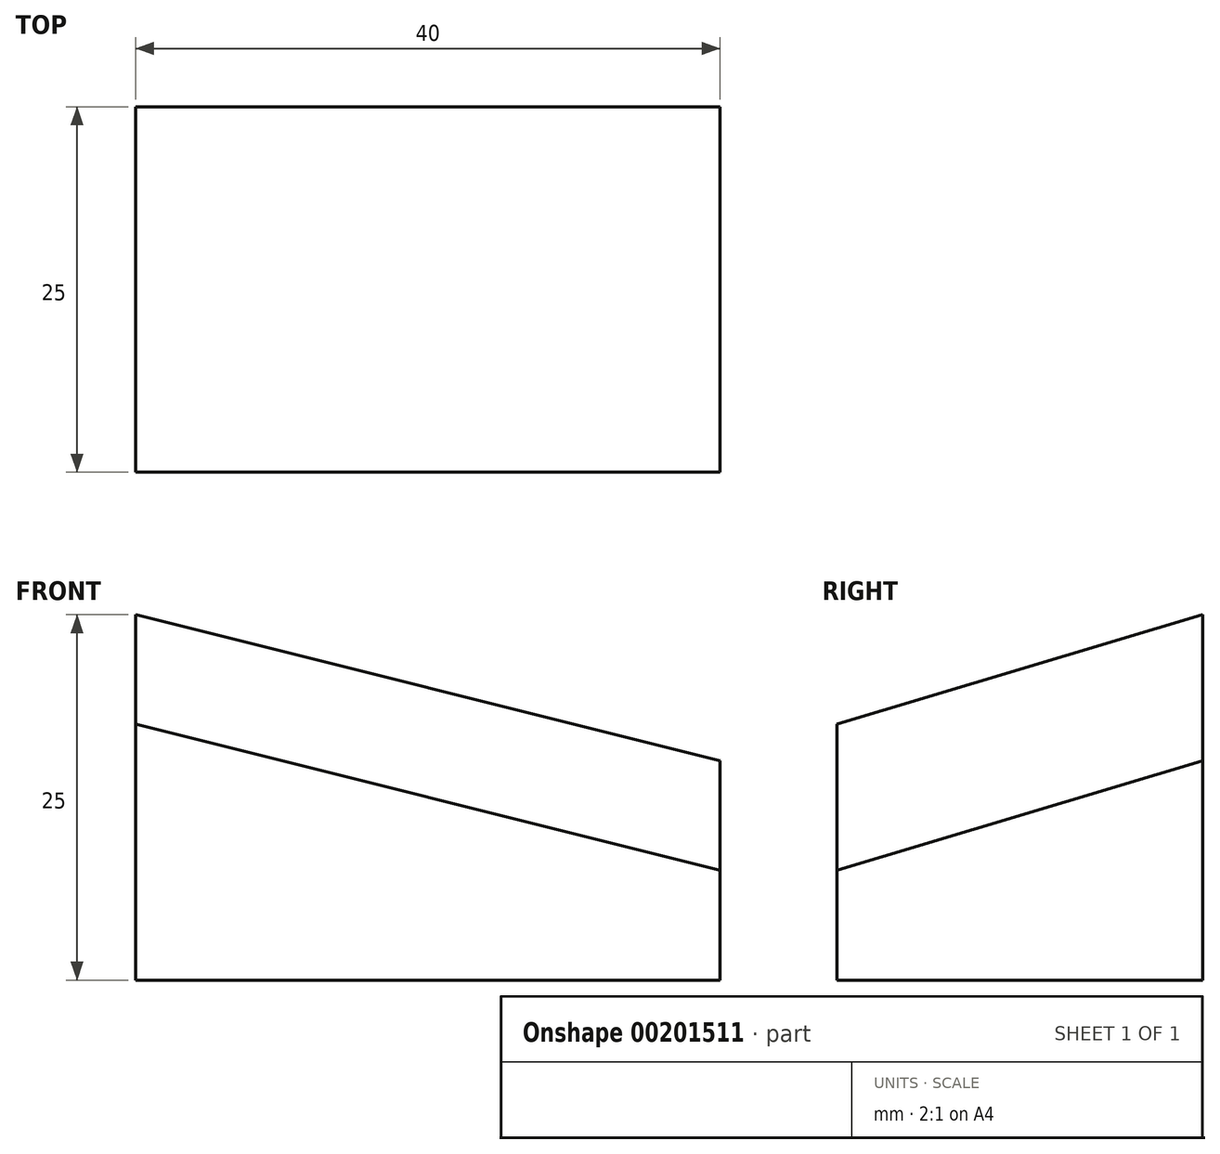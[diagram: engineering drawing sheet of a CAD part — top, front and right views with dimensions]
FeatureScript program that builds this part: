
annotation { "Feature Type Name" : "Feature", "Feature Type Description" : "" }
export const myFeature = defineFeature(function(context is Context, id is Id, definition is map)
    precondition{}
    {
        {
            var Q0;
            Q0=qCreatedBy(makeId("Front.planeOp"),FACE);
            var sketch = newSketch(context, id + "F0", { "sketchPlane" : qUnion([Q0])});
            skLineSegment(sketch, "E0", {"start": v(0, 0) * mm, "end": v(-40, 0) * mm});
            skLineSegment(sketch, "E1", {"start": v(-40, 0) * mm, "end": v(-40, 17.5) * mm});
            skLineSegment(sketch, "E2", {"start": v(-40, 17.5) * mm, "end": v(0, 7.5) * mm});
            skLineSegment(sketch, "E3", {"start": v(0, 7.5) * mm, "end": v(0, 0) * mm});
            skSolve(sketch);
        }
        {
            var Q0;
            Q0=qCreatedBy(makeId("Front.planeOp"),FACE);
            cPlane(context, id + "F1", {"entities" : qUnion([Q0]), "cplaneType" : CPlaneType.OFFSET, "offset" : 25 * mm, "oppositeDirection" : true, "width" : 150 * mm, "height" : 150 * mm});
        }
        {
            var Q0;
            Q0=qCreatedBy(id+"F1.planeOp",FACE);
            var sketch = newSketch(context, id + "F2", { "sketchPlane" : qUnion([Q0])});
            skLineSegment(sketch, "E4", {"start": v(0, 0) * mm, "end": v(-40, 0) * mm});
            skLineSegment(sketch, "E5", {"start": v(-40, 0) * mm, "end": v(-40, 25) * mm});
            skLineSegment(sketch, "E6", {"start": v(-40, 25) * mm, "end": v(0, 15) * mm});
            skLineSegment(sketch, "E7", {"start": v(0, 15) * mm, "end": v(0, 0) * mm});
            skSolve(sketch);
        }
        {
            var Q0;
            Q0=makeQuery(id+"F0.imprint","IMPRINT",FACE,{"disambiguationData":[TD([[makeQuery(id+"F0.imprint","IMPRINT",EDGE,{"derivedFrom":sQuery(id+"F0.wireOp",EDGE,"E0")}),-1.0]])]});
            var Q1;
            Q1=makeQuery(id+"F2.imprint","IMPRINT",FACE,{"disambiguationData":[TD([[makeQuery(id+"F2.imprint","IMPRINT",EDGE,{"derivedFrom":sQuery(id+"F2.wireOp",EDGE,"E4")}),-1.0]])]});
            loft(context, id + "F3", {"sheetProfilesArray" : [{ "sheetProfileEntities" : qUnion([Q0]) }, { "sheetProfileEntities" : qUnion([Q1]) }]});
        }
    });
